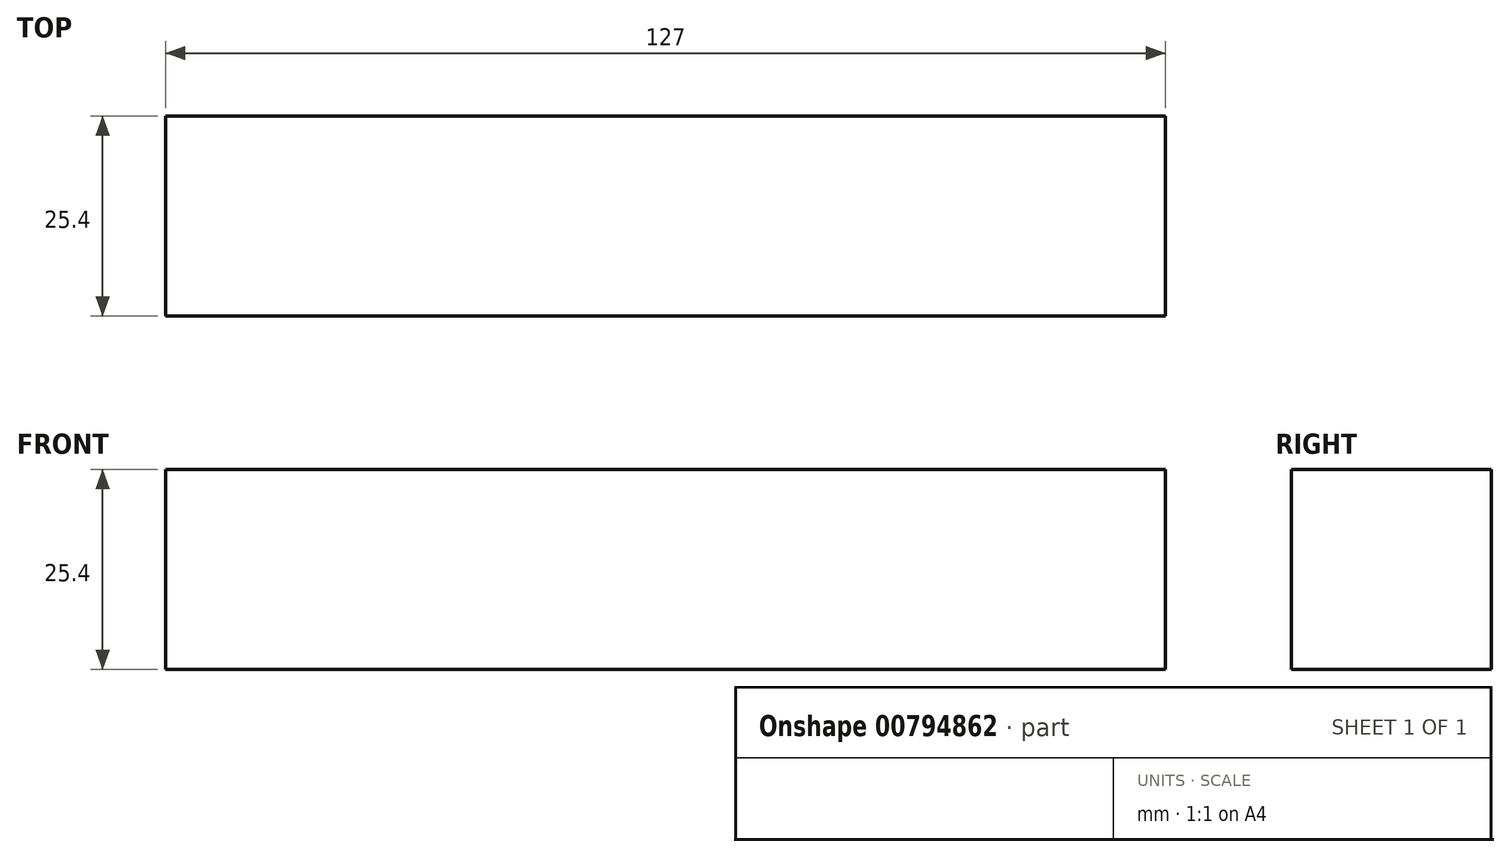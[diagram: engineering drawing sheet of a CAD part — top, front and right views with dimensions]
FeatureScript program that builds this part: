
annotation { "Feature Type Name" : "Feature", "Feature Type Description" : "" }
export const myFeature = defineFeature(function(context is Context, id is Id, definition is map)
    precondition{}
    {
        {
            var Q0;
            Q0=qCreatedBy(makeId("Right.planeOp"),FACE);
            var sketch = newSketch(context, id + "F0", { "sketchPlane" : qUnion([Q0])});
            skLineSegment(sketch, "E0.bottom", {"start": v(12.7, -12.7) * mm, "end": v(-12.7, -12.7) * mm});
            skLineSegment(sketch, "E0.top", {"start": v(12.7, 12.7) * mm, "end": v(-12.7, 12.7) * mm});
            skLineSegment(sketch, "E0.left", {"start": v(12.7, -12.7) * mm, "end": v(12.7, 12.7) * mm});
            skLineSegment(sketch, "E0.right", {"start": v(-12.7, -12.7) * mm, "end": v(-12.7, 12.7) * mm});
            skPoint(sketch, "E0.middle", {"position": v(0, 0) * mm});
            skSolve(sketch);
        }
        {
            var Q0;
            Q0 = qSketchRegion(id + "F0", true);
            extrude(context, id + "F1", {"entities" : qUnion([Q0]), "depth" : 127 * mm, "offsetDistance" : 25.4 * mm});
        }
    });
